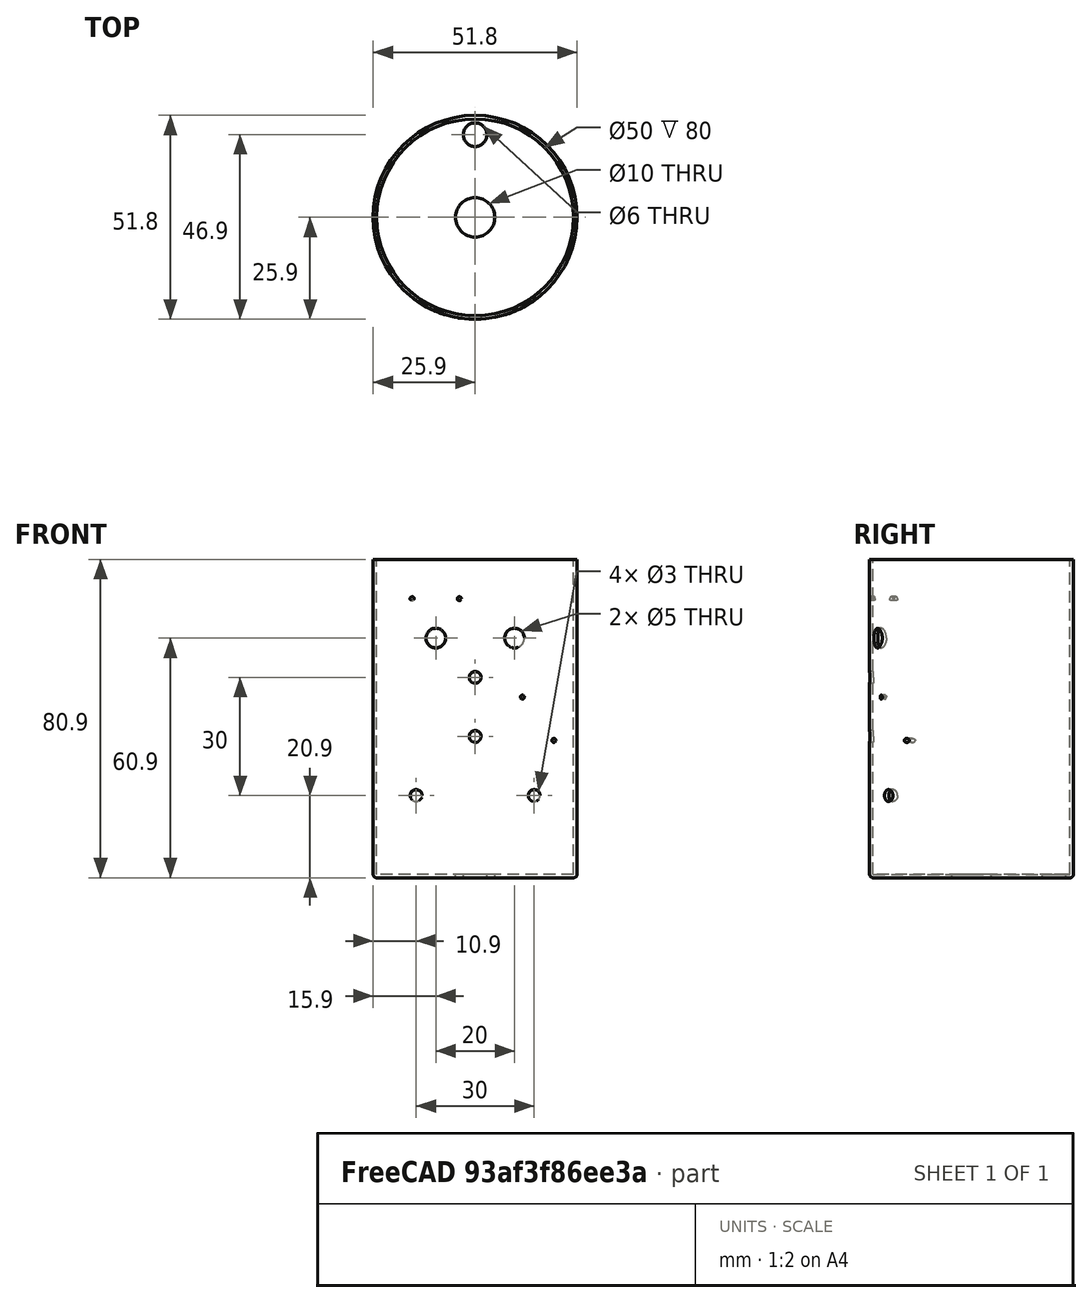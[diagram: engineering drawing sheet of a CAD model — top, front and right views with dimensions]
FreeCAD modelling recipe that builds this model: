
FCSTD DOCUMENT  (FreeCAD 0.16R6712 (Git))
Label: Franky_MakerVentura
License: CreativeCommons Attribution
LicenseURL: http://creativecommons.org/licenses/by/4.0/
objects: Part::Cylinder×7, Part::Feature×5, Part::Thickness×1, Part::Mirroring×1, Part::MultiFuse×1, Part::Cut×1
note: 16 computed .brp shape members not serialized (recipe doc carries the construction recipe); baked Part::Feature solids carry a one-line shape summary decoded from their .brp

FEATURE [Part::Cylinder] Cylinder  label="Cuerpo macizo"
  Angle = 360
  Height = 80
  Radius = 25
FEATURE [Part::Thickness] Thickness  label="Cuerpo vaciado"
  Faces = -> Cylinder [Face2]
  Intersection = false
  Join = 0
  Mode = 0
  SelfIntersection = false
  Value = 0.9
FEATURE [Part::Cylinder] Cylinder001  label="Master ojo"
  Angle = 360
  Height = 10
  Placement = pos=(10,-20,60) rot=(1,0,0;1.5708rad)
  Radius = 2.5
FEATURE [Part::Mirroring] Part__Mirroring  label="Master ojo (Mirror #1)"
  Base = (0,0,0)
  Normal = (1,0,0)
  Source = -> Cylinder001
FEATURE [Part::Cylinder] Cylinder002  label="nariz paso superior"
  Angle = 360
  Height = 10
  Placement = pos=(0,-20,50) rot=(1,0,0;1.5708rad)
  Radius = 1.5
FEATURE [Part::Feature] Cylinder002001  label="nariz paso inferior"
  Placement = pos=(0,-20,35) rot=(1,0,0;1.5708rad)
  shape: bbox 3 x 10 x 3 mm, 3 faces (baked)
FEATURE [Part::Cylinder] Cylinder002002  label="paso lateral boca"
  Angle = 360
  Height = 10
  Placement = pos=(15,-15,20) rot=(1,0,0;1.5708rad)
  Radius = 1.5
FEATURE [Part::Feature] Cylinder002002001  label="paso lateral simetrico boca"
  Placement = pos=(-15,-15,20) rot=(1,0,0;1.5708rad)
  shape: bbox 3 x 10 x 3 mm, 3 faces (baked)
FEATURE [Part::Cylinder] Cylinder002002002  label="paso 1 resistencia ceja"
  Angle = 360
  Height = 10
  Placement = pos=(-4,-20,70) rot=(1,0,0;1.5708rad)
  Radius = 0.5
FEATURE [Part::Feature] Cylinder002002002001  label="paso 2 resistencia ceja"
  Placement = pos=(-16,-16,70) rot=(1,0,0;1.5708rad)
  shape: bbox 1 x 10 x 1 mm, 3 faces (baked)
FEATURE [Part::Feature] Cylinder002002002002  label="paso 1 resistencia pomulo"
  Placement = pos=(12,-20,45) rot=(1,0,0;1.5708rad)
  shape: bbox 1 x 10 x 1 mm, 3 faces (baked)
FEATURE [Part::Feature] Cylinder002002002003  label="paso 2 resistencia pomulo"
  Placement = pos=(20,-13,34) rot=(1,0,0;1.5708rad)
  shape: bbox 1 x 10 x 1 mm, 3 faces (baked)
FEATURE [Part::Cylinder] Cylinder002002002004  label="vaciado soporte servomotor"
  Angle = 360
  Height = 10
  Placement = pos=(0,0,-5) rot=(0,0,1;0rad)
  Radius = 5
FEATURE [Part::Cylinder] Cylinder002002002005  label="Paso de cableado"
  Angle = 360
  Height = 10
  Placement = pos=(0,21,-5) rot=(0,0,1;0rad)
  Radius = 3
FEATURE [Part::MultiFuse] Fusion  label="Fusion vaciados"
  Shapes = -> [Cylinder002001,Cylinder002002002003,Cylinder002002001,Cylinder002002002001,Cylinder002002002002,Cylinder002002002004,Cylinder002002,Cylinder002002002,Cylinder002,Cylinder001,Part__Mirroring,Cylinder002002002005]
FEATURE [Part::Cut] Cut  label="Franky"
  Base = -> Thickness
  Tool = -> Fusion
